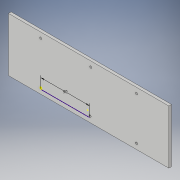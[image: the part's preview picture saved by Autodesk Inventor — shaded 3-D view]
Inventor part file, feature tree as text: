
AUTODESK INVENTOR PART (.ipt)
format: ipt  version: 2019 (Build 230136000, 136)  size: 133,632 bytes
history: native  units: mm
features: sketch x8, hole x6, extrude x1
ambient origin geometry x8: Origin, YZ Plane, XZ Plane, XY Plane, X Axis, Y Axis, Z Axis, Center Point
bodies: Solid1 (feature_tree)
feature tree (15):
  extrude  "Extrusion1"  Depth=5.0mm
  hole  "Hole1"  [1 undecoded]
  hole  "Hole2"  [1 undecoded]
  hole  "Hole3"  [1 undecoded]
  hole  "Hole4"  [1 undecoded]
  hole  "Hole5"  [1 undecoded]
  sketch  "Sketch7"  dims[d26=4.0mm d27=6.0mm d28=4.0mm d29=2.0mm d30=90.0deg d31=6.0mm d32=20.594885mm d33=60.0mm]
  hole  "Hole6"  [1 undecoded]
  sketch  "Sketch1"  dims[d2=5.0mm d3=0.0mm d4=60.0mm]
  sketch  "Sketch2"  dims[d5=10.0mm d6=10.0mm]
  sketch  "Sketch3"  dims[d7=4.0mm d8=6.0mm d9=4.0mm d10=2.0mm d11=90.0deg d12=6.0mm d13=20.594885mm d14=60.0mm]
  sketch  "Sketch4"  dims[d15=10.0mm]
  sketch  "Sketch5"  dims[d16=4.0mm d17=6.0mm d18=4.0mm d19=2.0mm d20=90.0deg d21=6.0mm d22=20.594885mm d23=60000.0mm]
  sketch  "Sketch6"  dims[d24=60.0mm d25=10.0mm]
  sketch  "Sketch8"  dims[d34=10.0mm d35=4.0mm d36=6.0mm d37=4.0mm d38=2.0mm d39=90.0deg d40=6.0mm d41=20.594885mm d42=90.0mm d43=4.0mm d44=6.0mm d45=4.0mm d46=2.0mm d47=90.0deg d48=6.0mm d49=20.594885mm d50=90.0mm d51=4.0mm d52=6.0mm d53=4.0mm d54=2.0mm d55=90.0deg d56=6.0mm d57=20.594885mm]
note: 6 required parameter values undecoded (feature->parameter linkage not recoverable at this tier; creation-order binding heuristic only, values carry confidence <= 0.55)
